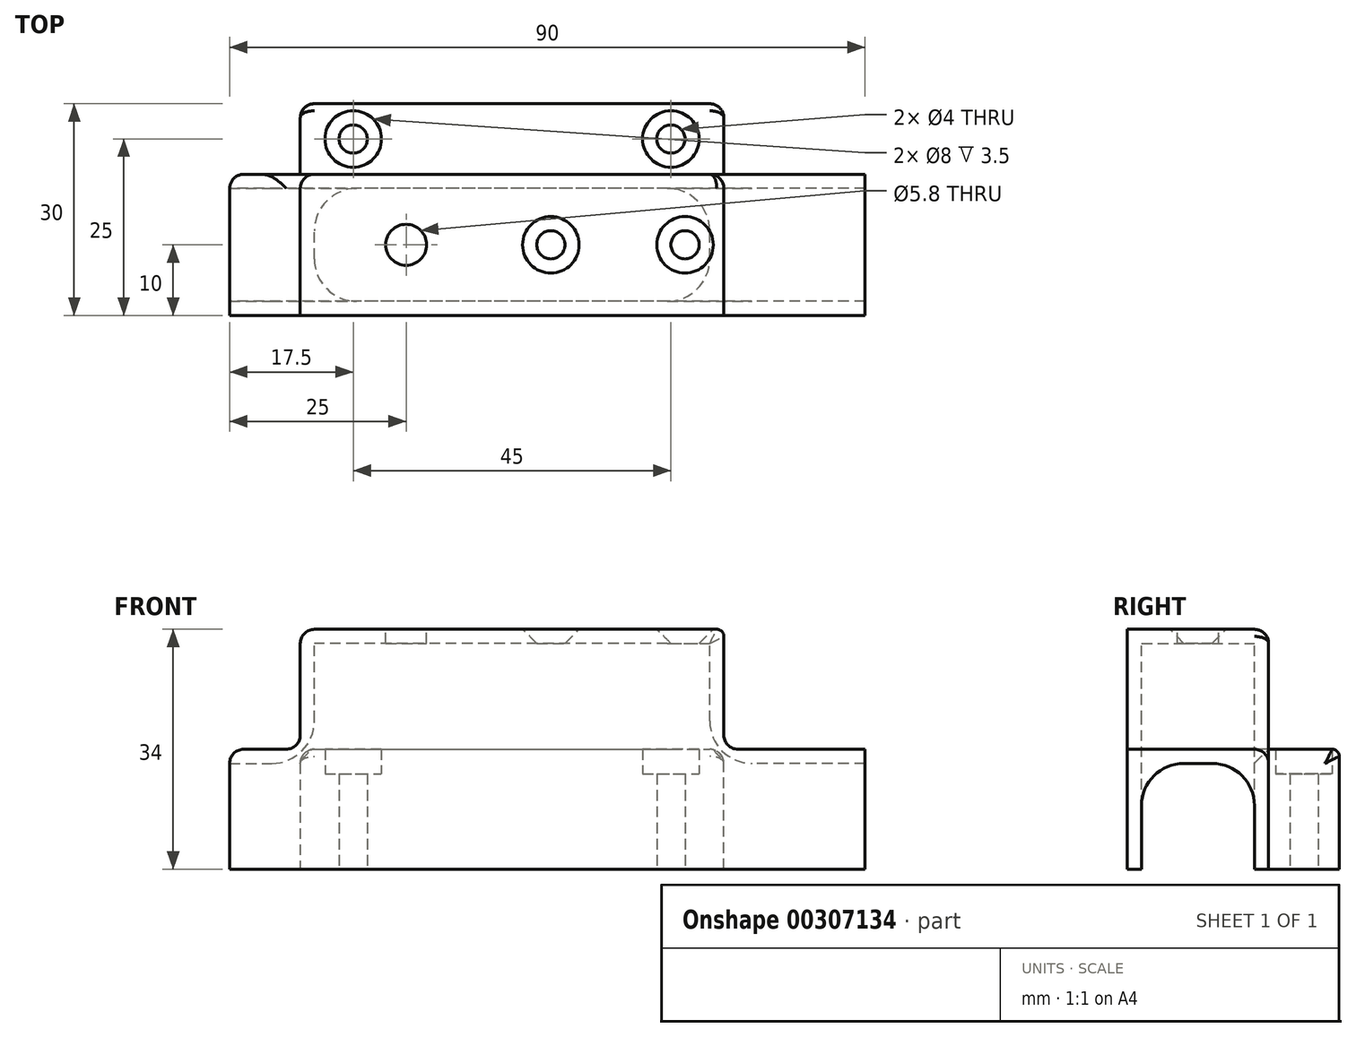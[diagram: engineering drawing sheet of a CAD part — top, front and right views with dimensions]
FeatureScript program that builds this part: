
annotation { "Feature Type Name" : "Feature", "Feature Type Description" : "" }
export const myFeature = defineFeature(function(context is Context, id is Id, definition is map)
    precondition{}
    {
        {
            var Q0;
            Q0=qCreatedBy(makeId("Front.planeOp"),FACE);
            var sketch = newSketch(context, id + "F0", { "sketchPlane" : qUnion([Q0])});
            skLineSegment(sketch, "E0", {"start": v(0, 0) * mm, "end": v(-40, 0) * mm});
            skLineSegment(sketch, "E1", {"start": v(-40, 0) * mm, "end": v(-40, 17) * mm});
            skLineSegment(sketch, "E2", {"start": v(-40, 17) * mm, "end": v(-30, 17) * mm});
            skLineSegment(sketch, "E3", {"start": v(-30, 17) * mm, "end": v(-30, 34) * mm});
            skLineSegment(sketch, "E4", {"start": v(-30, 34) * mm, "end": v(0, 34) * mm});
            skLineSegment(sketch, "E5.MirrorCS", {"start": v(30, 34) * mm, "end": v(0, 34) * mm});
            skLineSegment(sketch, "E6.MirrorCS", {"start": v(30, 17) * mm, "end": v(30, 34) * mm});
            skLineSegment(sketch, "E7.MirrorCS", {"start": v(50, 17) * mm, "end": v(30, 17) * mm});
            skLineSegment(sketch, "E8.MirrorCS", {"start": v(50, 0) * mm, "end": v(50, 17) * mm});
            skLineSegment(sketch, "E9.MirrorCS", {"start": v(0, 0) * mm, "end": v(50, 0) * mm});
            skLineSegment(sketch, "E10", {"start": v(-30, 17) * mm, "end": v(30, 17) * mm});
            skLineSegment(sketch, "E11", {"start": v(30, 0) * mm, "end": v(30, 17) * mm});
            skLineSegment(sketch, "E12", {"start": v(-30, 17) * mm, "end": v(-30, 0) * mm});
            skSolve(sketch);
        }
        {
            var Q0;
            Q0=qSketchRegion(id+"F0",true);
            var Q1;
            Q1=makeQuery(id+"F0.imprint","IMPRINT",FACE,{"disambiguationData":[TD([[makeQuery(id+"F0.imprint","IMPRINT",EDGE,{"derivedFrom":sQuery(id+"F0.wireOp",EDGE,"E0")}),-1.0]])]});
            extrude(context, id + "F1", {"entities" : qUnion([Q0, Q1]), "depth" : 20 * mm});
        }
        {
            var Q0;
            Q0=makeQuery(id+"F1.opExtrude","SWEPT_FACE",FACE,{"disambiguationData":[OSD([sQuery(id+"F0.wireOp",EDGE,"E0"),sQuery(id+"F0.wireOp",EDGE,"E9.MirrorCS")])]});
            shell(context, id + "F2", {"entities" : qUnion([Q0]), "thickness" : 2 * mm});
        }
        {
            var Q0;
            Q0=makeQuery(id+"F1.opExtrude","SWEPT_FACE",FACE,{"disambiguationData":[OSD([sQuery(id+"F0.wireOp",EDGE,"E4"),sQuery(id+"F0.wireOp",EDGE,"E5.MirrorCS")])]});
            var sketch = newSketch(context, id + "F3", { "sketchPlane" : qUnion([Q0])});
            skLineSegment(sketch, "E13", {"start": v(0, 0) * mm, "end": v(0, -20) * mm});
            skLineSegment(sketch, "E14", {"start": v(0, -10) * mm, "end": v(-30, -10) * mm});
            skCircle(sketch, "E15", {"center": v(-15, -10) * mm, "radius": 2.9 * mm});
            skLineSegment(sketch, "E16.MirrorCS", {"start": v(0, -10) * mm, "end": v(30, -10) * mm});
            skLineSegment(sketch, "E17", {"start": v(15, -10) * mm, "end": v(11, -10) * mm});
            skLineSegment(sketch, "E18", {"start": v(11, -10) * mm, "end": v(11, -6.5) * mm});
            skLineSegment(sketch, "E19", {"start": v(11, -6.5) * mm, "end": v(15, -6.5) * mm});
            skLineSegment(sketch, "E20", {"start": v(15, -10) * mm, "end": v(15, -8.98) * mm});
            skLineSegment(sketch, "E21.MirrorCS", {"start": v(19, -10) * mm, "end": v(19, -6.5) * mm});
            skLineSegment(sketch, "E22.MirrorCS", {"start": v(19, -6.5) * mm, "end": v(15, -6.5) * mm});
            skLineSegment(sketch, "E23.MirrorCS", {"start": v(11, -10) * mm, "end": v(11, -13.5) * mm});
            skLineSegment(sketch, "E24.MirrorCS", {"start": v(11, -13.5) * mm, "end": v(15, -13.5) * mm});
            skLineSegment(sketch, "E25.MirrorCS", {"start": v(19, -13.5) * mm, "end": v(15, -13.5) * mm});
            skLineSegment(sketch, "E26.MirrorCS", {"start": v(19, -10) * mm, "end": v(19, -13.5) * mm});
            skLineSegment(sketch, "E27", {"start": v(19, -10) * mm, "end": v(30, -10) * mm});
            skLineSegment(sketch, "E28", {"start": v(24.5, -10) * mm, "end": v(24.5, -8.9) * mm});
            skLineSegment(sketch, "E29", {"start": v(11, -10) * mm, "end": v(0, -10) * mm});
            skLineSegment(sketch, "E30", {"start": v(5.5, -10) * mm, "end": v(5.5, -8.97) * mm});
            skSolve(sketch);
        }
        {
            var Q0;
            {var subQ0=sQuery(id+"F3.wireOp",EDGE,"E15");var subQ1=sQuery(id+"F3.wireOp",EDGE,"E14");var subQ2=makeQuery(id+"F3.imprint","INTERSECT",VERTEX,{"disambiguationData":[OD(0.0)],"derivedFrom":[subQ1,subQ0]});Q0=makeQuery(id+"F3.imprint","IMPRINT",FACE,{"disambiguationData":[TD([[makeQuery(id+"F3.imprint","IMPRINT",EDGE,{"disambiguationData":[TD([[subQ2,-1.0]])],"derivedFrom":subQ1}),1.0]])]});}
            var Q1;
            {var subQ0=sQuery(id+"F3.wireOp",EDGE,"E17");Q1=makeQuery(id+"F3.imprint","IMPRINT",FACE,{"disambiguationData":[TD([[makeQuery(id+"F3.imprint","IMPRINT",EDGE,{"derivedFrom":subQ0}),-1.0]])]});}
            var Q2;
            {var subQ0=sQuery(id+"F3.wireOp",EDGE,"E17");Q2=makeQuery(id+"F3.imprint","IMPRINT",FACE,{"disambiguationData":[TD([[makeQuery(id+"F3.imprint","IMPRINT",EDGE,{"derivedFrom":subQ0}),1.0]])]});}
            var Q3;
            {var subQ0=sQuery(id+"F3.wireOp",EDGE,"E15");var subQ1=sQuery(id+"F3.wireOp",EDGE,"E14");var subQ2=makeQuery(id+"F3.imprint","INTERSECT",VERTEX,{"disambiguationData":[OD(0.0)],"derivedFrom":[subQ1,subQ0]});Q3=makeQuery(id+"F3.imprint","IMPRINT",FACE,{"disambiguationData":[TD([[makeQuery(id+"F3.imprint","IMPRINT",EDGE,{"disambiguationData":[TD([[subQ2,-1.0]])],"derivedFrom":subQ1}),-1.0]])]});}
            extrude(context, id + "F4", {"entities" : qUnion([Q0, Q1, Q2, Q3]), "operationType" : NewBodyOperationType.REMOVE, "oppositeDirection" : true, "depth" : 3 * mm});
        }
        {
            var Q0;
            Q0=makeQuery(id+"F2.opShell","OFFSET_FACE",FACE,{"disambiguationData":[OSD([sQuery(id+"F0.wireOp",EDGE,"E8.MirrorCS")])]});
            extrude(context, id + "F5", {"entities" : qUnion([Q0]), "operationType" : NewBodyOperationType.REMOVE, "oppositeDirection" : true, "depth" : 25 * mm});
        }
        {
            var Q0;
            Q0=makeQuery(id+"F2.opShell","OFFSET_EDGE",EDGE,{"disambiguationData":[OSD([sQuery(id+"F0.wireOp",EDGE,"E6.MirrorCS"),sQuery(id+"F0.wireOp",EDGE,"E7.MirrorCS")])]});
            var Q1;
            Q1=makeQuery(id+"F2.opShell","OFFSET_EDGE",EDGE,{"disambiguationData":[OSD([sQuery(id+"F0.wireOp",EDGE,"E2"),sQuery(id+"F0.wireOp",EDGE,"E3")])]});
            fillet(context, id + "F6", {"entities" : qUnion([Q0, Q1]), "radius" : 6 * mm, "tangentPropagation" : true, "allowEdgeOverflow" : false});
        }
        {
            var Q0;
            Q0=makeQuery(id+"F1.opExtrude","SWEPT_EDGE",EDGE,{"disambiguationData":[OSD([sQuery(id+"F0.wireOp",EDGE,"E3"),sQuery(id+"F0.wireOp",EDGE,"E4")])]});
            var Q1;
            Q1=makeQuery(id+"F1.opExtrude","SWEPT_EDGE",EDGE,{"disambiguationData":[OSD([sQuery(id+"F0.wireOp",EDGE,"E1"),sQuery(id+"F0.wireOp",EDGE,"E2")])]});
            var Q2;
            Q2=makeQuery(id+"F1.opExtrude","SWEPT_EDGE",EDGE,{"disambiguationData":[OSD([sQuery(id+"F0.wireOp",EDGE,"E2"),sQuery(id+"F0.wireOp",EDGE,"E3")])]});
            var Q3;
            Q3=makeQuery(id+"F1.opExtrude","CAP_EDGE",EDGE,{"disambiguationData":[OSD([sQuery(id+"F0.wireOp",EDGE,"E4"),sQuery(id+"F0.wireOp",EDGE,"E5.MirrorCS")])],"isStart":true});
            var Q4;
            Q4=makeQuery(id+"F1.opExtrude","CAP_EDGE",EDGE,{"disambiguationData":[OSD([sQuery(id+"F0.wireOp",EDGE,"E6.MirrorCS")])],"isStart":true});
            var Q5;
            Q5=makeQuery(id+"F1.opExtrude","CAP_EDGE",EDGE,{"disambiguationData":[OSD([sQuery(id+"F0.wireOp",EDGE,"E7.MirrorCS")])],"isStart":true});
            var Q6;
            Q6=makeQuery(id+"F1.opExtrude","SWEPT_EDGE",EDGE,{"disambiguationData":[OSD([sQuery(id+"F0.wireOp",EDGE,"E6.MirrorCS"),sQuery(id+"F0.wireOp",EDGE,"E7.MirrorCS")])]});
            var Q7;
            Q7=makeQuery(id+"F1.opExtrude","CAP_EDGE",EDGE,{"disambiguationData":[OSD([sQuery(id+"F0.wireOp",EDGE,"E3")])],"isStart":true});
            var Q8;
            Q8=makeQuery(id+"F1.opExtrude","CAP_EDGE",EDGE,{"disambiguationData":[OSD([sQuery(id+"F0.wireOp",EDGE,"E1")])],"isStart":true});
            fillet(context, id + "F7", {"entities" : qUnion([Q0, Q1, Q2, Q3, Q4, Q5, Q6, Q7, Q8]), "radius" : 2 * mm, "tangentPropagation" : true, "allowEdgeOverflow" : false});
        }
        {
            var Q0;
            Q0=sQuery(id+"F3.wireOp",VERTEX,"E30.start");
            var Q1;
            Q1=sQuery(id+"F3.wireOp",VERTEX,"E28.start");
            var Q2;
            Q2=makeQuery(id+"F1.opExtrude","SWEPT_BODY",BODY,{"disambiguationData":[OSD([sQuery(id+"F0.wireOp",EDGE,"E0"),sQuery(id+"F0.wireOp",EDGE,"E1"),sQuery(id+"F0.wireOp",EDGE,"E2"),sQuery(id+"F0.wireOp",EDGE,"E3"),sQuery(id+"F0.wireOp",EDGE,"E4"),sQuery(id+"F0.wireOp",EDGE,"E5.MirrorCS"),sQuery(id+"F0.wireOp",EDGE,"E6.MirrorCS"),sQuery(id+"F0.wireOp",EDGE,"E7.MirrorCS"),sQuery(id+"F0.wireOp",EDGE,"E8.MirrorCS"),sQuery(id+"F0.wireOp",EDGE,"E9.MirrorCS")])]});
            hole(context, id + "F8", {"style" : HoleStyle.C_SINK, "endStyle" : HoleEndStyle.THROUGH, "holeDiameter" : 2.6 * mm, "cSinkDiameter" : 8 * mm, "cSinkAngle" : 90 * degree, "tappedDepth" : 12 * mm, "tapClearance" : 3, "locations" : qUnion([Q0, Q1]), "scope" : qUnion([Q2]), "startStyle" : HoleStartStyle.PART});
        }
        {
            var Q0;
            Q0=makeQuery(id+"F1.opExtrude","SWEPT_EDGE",EDGE,{"disambiguationData":[OSD([sQuery(id+"F0.wireOp",EDGE,"E5.MirrorCS"),sQuery(id+"F0.wireOp",EDGE,"E6.MirrorCS")])]});
            fillet(context, id + "F9", {"entities" : qUnion([Q0]), "radius" : 1 * mm, "tangentPropagation" : true, "allowEdgeOverflow" : false});
        }
        {
            var Q0;
            Q0=makeQuery(id+"F0.imprint","IMPRINT",FACE,{"disambiguationData":[TD([[makeQuery(id+"F0.imprint","IMPRINT",EDGE,{"derivedFrom":sQuery(id+"F0.wireOp",EDGE,"E10")}),-1.0]])]});
            extrude(context, id + "F10", {"entities" : qUnion([Q0]), "operationType" : NewBodyOperationType.ADD, "oppositeDirection" : true, "depth" : 10 * mm});
        }
        {
            var Q0;
            Q0=makeQuery(id+"F10.opExtrude","SWEPT_FACE",FACE,{"disambiguationData":[OSD([sQuery(id+"F0.wireOp",EDGE,"E10")])]});
            var sketch = newSketch(context, id + "F11", { "sketchPlane" : qUnion([Q0])});
            skLineSegment(sketch, "E31", {"start": v(-30, 5) * mm, "end": v(30, 5) * mm});
            skLineSegment(sketch, "E32", {"start": v(30, 5) * mm, "end": v(0, 5) * mm});
            skLineSegment(sketch, "E33", {"start": v(0, 5) * mm, "end": v(-30, 5) * mm});
            skLineSegment(sketch, "E34", {"start": v(-15, 5) * mm, "end": v(-30, 5) * mm});
            skLineSegment(sketch, "E35", {"start": v(-22.5, 5) * mm, "end": v(-22.5, 8) * mm});
            skLineSegment(sketch, "E36", {"start": v(30, 5) * mm, "end": v(22.5, 5) * mm});
            skSolve(sketch);
        }
        {
            var Q0;
            Q0=sQuery(id+"F11.wireOp",VERTEX,"E35.start");
            var Q1;
            Q1=sQuery(id+"F11.wireOp",VERTEX,"E36.end");
            var Q2;
            Q2=makeQuery(id+"F1.opExtrude","SWEPT_BODY",BODY,{"disambiguationData":[OSD([sQuery(id+"F0.wireOp",EDGE,"E0"),sQuery(id+"F0.wireOp",EDGE,"E1"),sQuery(id+"F0.wireOp",EDGE,"E2"),sQuery(id+"F0.wireOp",EDGE,"E3"),sQuery(id+"F0.wireOp",EDGE,"E4"),sQuery(id+"F0.wireOp",EDGE,"E5.MirrorCS"),sQuery(id+"F0.wireOp",EDGE,"E6.MirrorCS"),sQuery(id+"F0.wireOp",EDGE,"E7.MirrorCS"),sQuery(id+"F0.wireOp",EDGE,"E8.MirrorCS"),sQuery(id+"F0.wireOp",EDGE,"E9.MirrorCS")])]});
            hole(context, id + "F12", {"style" : HoleStyle.C_BORE, "endStyle" : HoleEndStyle.THROUGH, "holeDiameter" : 4 * mm, "cBoreDiameter" : 8 * mm, "cBoreDepth" : 3.5 * mm, "tappedDepth" : 12 * mm, "tapClearance" : 3, "locations" : qUnion([Q0, Q1]), "scope" : qUnion([Q2]), "startStyle" : HoleStartStyle.PART});
        }
        {
            var Q0;
            Q0=makeQuery(id+"F10.opExtrude","SWEPT_EDGE",EDGE,{"disambiguationData":[OSD([sQuery(id+"F0.wireOp",EDGE,"E6.MirrorCS"),sQuery(id+"F0.wireOp",EDGE,"E7.MirrorCS"),sQuery(id+"F0.wireOp",EDGE,"E10"),sQuery(id+"F0.wireOp",EDGE,"E11")])]});
            var Q1;
            Q1=makeQuery(id+"F10.opExtrude","CAP_EDGE",EDGE,{"disambiguationData":[OSD([sQuery(id+"F0.wireOp",EDGE,"E11")])],"isStart":false});
            var Q2;
            Q2=makeQuery(id+"F10.opExtrude","SWEPT_EDGE",EDGE,{"disambiguationData":[OSD([sQuery(id+"F0.wireOp",EDGE,"E2"),sQuery(id+"F0.wireOp",EDGE,"E3"),sQuery(id+"F0.wireOp",EDGE,"E10"),sQuery(id+"F0.wireOp",EDGE,"E12")])]});
            var Q3;
            Q3=makeQuery(id+"F10.opExtrude","CAP_EDGE",EDGE,{"disambiguationData":[OSD([sQuery(id+"F0.wireOp",EDGE,"E12")])],"isStart":false});
            fillet(context, id + "F13", {"entities" : qUnion([Q0, Q1, Q2, Q3]), "radius" : 2 * mm, "tangentPropagation" : true, "allowEdgeOverflow" : false});
        }
        {
            var Q0;
            Q0=makeQuery(id+"F10.opExtrude","CAP_EDGE",EDGE,{"disambiguationData":[OSD([sQuery(id+"F0.wireOp",EDGE,"E10")])],"isStart":false});
            fillet(context, id + "F14", {"entities" : qUnion([Q0]), "radius" : 1 * mm, "tangentPropagation" : true, "allowEdgeOverflow" : false});
        }
        {
            var Q0;
            Q0=makeQuery(id+"F2.opShell","OFFSET_FACE",FACE,{"disambiguationData":[OSD([sQuery(id+"F0.wireOp",EDGE,"E1")])]});
            extrude(context, id + "F15", {"entities" : qUnion([Q0]), "operationType" : NewBodyOperationType.REMOVE, "oppositeDirection" : true, "depth" : 25 * mm});
        }
    });
